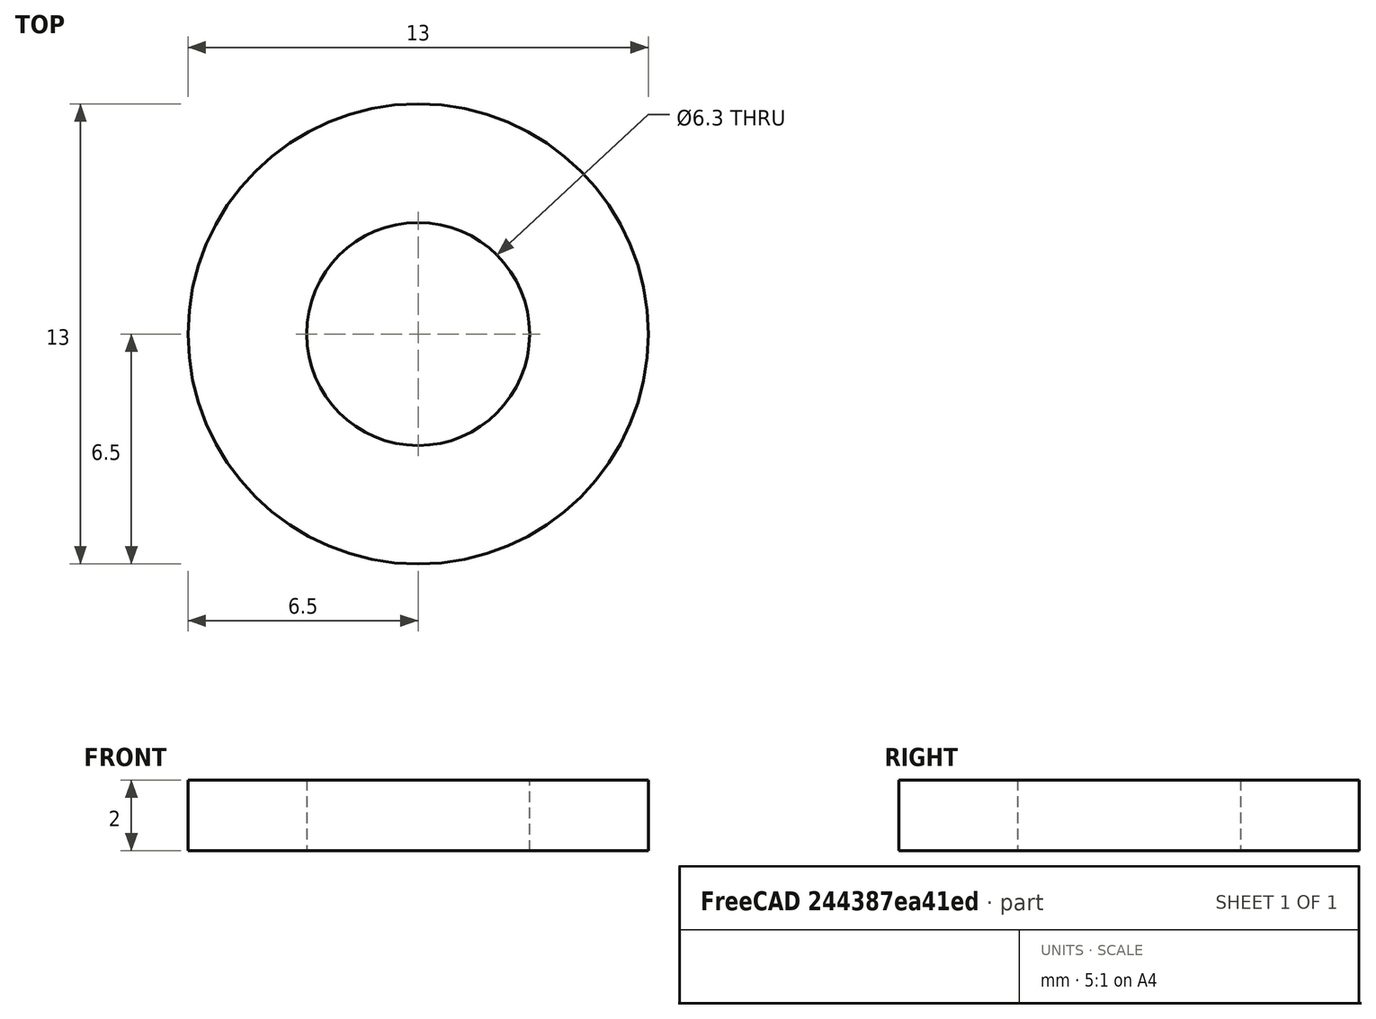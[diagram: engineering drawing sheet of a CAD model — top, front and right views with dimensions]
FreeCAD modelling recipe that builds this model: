
FCSTD DOCUMENT  (FreeCAD 0.20R25288 (Git))
Label: bike mud washer
License: All rights reserved
LicenseURL: http://en.wikipedia.org/wiki/All_rights_reserved
objects: Sketcher::SketchObject×1, PartDesign::Pad×1, PartDesign::Body×1
note: 4 computed .brp shape members not serialized (recipe doc carries the construction recipe); baked Part::Feature solids carry a one-line shape summary decoded from their .brp

FEATURE [Sketcher::SketchObject] Sketch
  FullyConstrained = true
  MapMode = 5
  Support = -> [XY_Plane]
  sketch-geometry (2):
    g0: Circle CenterX=0 CenterY=0 CenterZ=0 NormalX=0 NormalY=0 NormalZ=1 AngleXU=0 Radius=3.15
    g1: Circle CenterX=0 CenterY=0 CenterZ=0 NormalX=0 NormalY=0 NormalZ=1 AngleXU=0 Radius=6.5
  constraints (4):
    c: Coincident(g0,g-1)
    c: Tangent(g1,g0) = -1.5708
    c: Diameter(g1) = 13
    c: Diameter(g0) = 6.3
FEATURE [PartDesign::Pad] Pad
  Direction = (0,0,1)
  Length = 2
  Length2 = 100
  Profile = -> Sketch
  Refine = true
  Type = 0
FEATURE [PartDesign::Body] Body
  Group = -> [Sketch,Pad]
  Origin = -> Origin
  Tip = -> Pad
